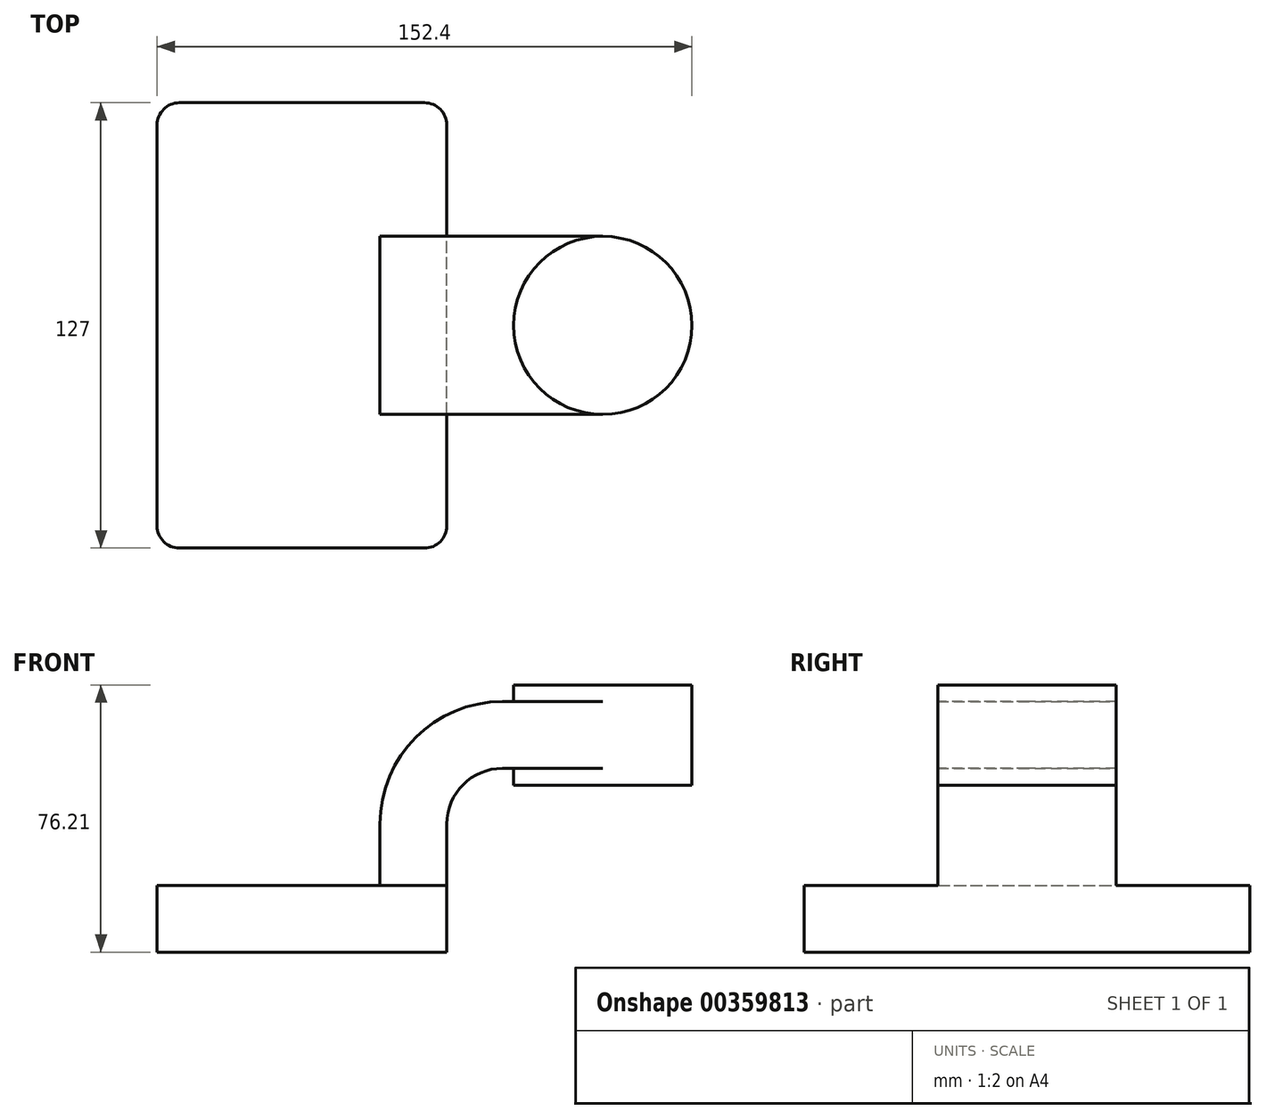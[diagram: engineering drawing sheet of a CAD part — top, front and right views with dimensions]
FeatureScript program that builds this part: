
annotation { "Feature Type Name" : "Feature", "Feature Type Description" : "" }
export const myFeature = defineFeature(function(context is Context, id is Id, definition is map)
    precondition{}
    {
        {
            var Q0;
            Q0=qCreatedBy(makeId("Front.planeOp"),FACE);
            var sketch = newSketch(context, id + "F0", { "sketchPlane" : qUnion([Q0])});
            skLineSegment(sketch, "E0.bottom", {"start": v(-41.28, -9.53) * mm, "end": v(41.28, -9.53) * mm});
            skLineSegment(sketch, "E0.top", {"start": v(-41.28, 9.52) * mm, "end": v(41.28, 9.52) * mm});
            skLineSegment(sketch, "E0.left", {"start": v(-41.28, -9.53) * mm, "end": v(-41.28, 9.52) * mm});
            skLineSegment(sketch, "E0.right", {"start": v(41.28, -9.53) * mm, "end": v(41.28, 9.52) * mm});
            skPoint(sketch, "E0.middle", {"position": v(0, 0) * mm});
            skLineSegment(sketch, "E1.bottom", {"start": v(60.32, 38.1) * mm, "end": v(111.12, 38.1) * mm});
            skLineSegment(sketch, "E1.top", {"start": v(60.32, 66.67) * mm, "end": v(111.12, 66.67) * mm});
            skLineSegment(sketch, "E1.left", {"start": v(60.32, 38.1) * mm, "end": v(60.32, 66.67) * mm});
            skLineSegment(sketch, "E1.right", {"start": v(111.12, 38.1) * mm, "end": v(111.12, 66.67) * mm});
            skPoint(sketch, "E1.middle", {"position": v(85.72, 52.39) * mm});
            skLineSegment(sketch, "E2", {"start": v(41.27, 9.52) * mm, "end": v(41.27, 27) * mm});
            skArc(sketch, "E3", {"start": v(41.27, 27) * mm, "mid": v(45.92, 38.23) * mm, "end": v(57.15, 42.88) * mm});
            skLineSegment(sketch, "E4", {"start": v(57.15, 42.88) * mm, "end": v(85.72, 42.88) * mm});
            skLineSegment(sketch, "E5.0", {"start": v(57.15, 61.93) * mm, "end": v(85.72, 61.93) * mm});
            skArc(sketch, "E5.1", {"start": v(22.22, 27) * mm, "mid": v(32.45, 51.7) * mm, "end": v(57.15, 61.93) * mm});
            skLineSegment(sketch, "E5.2", {"start": v(22.22, 9.52) * mm, "end": v(22.22, 27) * mm});
            skLineSegment(sketch, "E6", {"start": v(85.72, 38.1) * mm, "end": v(85.72, 66.67) * mm});
            skFitSpline(sketch, "E7", {"points": [v(-41.28, 9.52) * mm, v(57.15, 61.93) * mm], "startDerivative": vector(0, 104.85) * mm, "endDerivative": vector(171.45, -8.27) * mm});
            skSolve(sketch);
        }
        {
            var Q0;
            Q0=makeQuery(id+"F0.imprint","IMPRINT",FACE,{"disambiguationData":[TD([[makeQuery(id+"F0.imprint","IMPRINT",EDGE,{"derivedFrom":sQuery(id+"F0.wireOp",EDGE,"E0.bottom")}),1.0]])]});
            extrude(context, id + "F1", {"entities" : qUnion([Q0]), "endBound" : BoundingType.SYMMETRIC, "depth" : 127 * mm});
        }
        {
            var Q0;
            {var subQ1=sQuery(id+"F0.wireOp",EDGE,"E2");Q0=makeQuery(id+"F0.imprint","IMPRINT",FACE,{"disambiguationData":[TD([[makeQuery(id+"F0.imprint","IMPRINT",EDGE,{"derivedFrom":subQ1}),1.0]])]});}
            var Q1;
            {var subQ0=sQuery(id+"F0.wireOp",EDGE,"E4");var subQ1=sQuery(id+"F0.wireOp",EDGE,"E1.left");var subQ2=makeQuery(id+"F0.imprint","INTERSECT",VERTEX,{"derivedFrom":[subQ1,subQ0]});Q1=makeQuery(id+"F0.imprint","IMPRINT",FACE,{"disambiguationData":[TD([[makeQuery(id+"F0.imprint","IMPRINT",EDGE,{"disambiguationData":[TD([[subQ2,-1.0]])],"derivedFrom":subQ1}),-1.0]])]});}
            extrude(context, id + "F2", {"entities" : qUnion([Q0, Q1]), "operationType" : NewBodyOperationType.ADD, "endBound" : BoundingType.SYMMETRIC, "depth" : 50.8 * mm});
        }
        {
            var Q0;
            Q0=makeQuery(id+"F0.imprint","IMPRINT",FACE,{"disambiguationData":[TD([[makeQuery(id+"F0.imprint","IMPRINT",EDGE,{"derivedFrom":sQuery(id+"F0.wireOp",EDGE,"E5.1")}),1.0]])]});
            extrude(context, id + "F3", {"entities" : qUnion([Q0]), "operationType" : NewBodyOperationType.ADD, "endBound" : BoundingType.SYMMETRIC, "depth" : 15.88 * mm});
        }
        {
            var Q0;
            {var subQ0=sQuery(id+"F0.wireOp",EDGE,"E1.right");Q0=makeQuery(id+"F0.imprint","IMPRINT",FACE,{"disambiguationData":[TD([[makeQuery(id+"F0.imprint","IMPRINT",EDGE,{"derivedFrom":subQ0}),1.0]])]});}
            var Q1;
            Q1=sQuery(id+"F0.wireOp",EDGE,"E6");
            var Q2;
            Q2=sQuery(id+"F0.wireOp",EDGE,"E6");
            revolve(context, id + "F4", {"operationType" : NewBodyOperationType.ADD, "entities" : qUnion([Q0]), "surfaceEntities" : qUnion([Q1]), "axis" : qUnion([Q2]), "revolveType" : RevolveType.FULL});
        }
        {
            var Q0;
            Q0=makeQuery(id+"F1.opExtrude","CAP_EDGE",EDGE,{"disambiguationData":[OSD([sQuery(id+"F0.wireOp",EDGE,"E0.right")])],"isStart":false});
            var Q1;
            Q1=makeQuery(id+"F1.opExtrude","CAP_EDGE",EDGE,{"disambiguationData":[OSD([sQuery(id+"F0.wireOp",EDGE,"E0.left")])],"isStart":false});
            var Q2;
            Q2=makeQuery(id+"F1.opExtrude","CAP_EDGE",EDGE,{"disambiguationData":[OSD([sQuery(id+"F0.wireOp",EDGE,"E0.right")])],"isStart":true});
            var Q3;
            Q3=makeQuery(id+"F1.opExtrude","CAP_EDGE",EDGE,{"disambiguationData":[OSD([sQuery(id+"F0.wireOp",EDGE,"E0.left")])],"isStart":true});
            fillet(context, id + "F5", {"entities" : qUnion([Q0, Q1, Q2, Q3]), "radius" : 6.35 * mm, "tangentPropagation" : true, "allowEdgeOverflow" : false});
        }
    });
